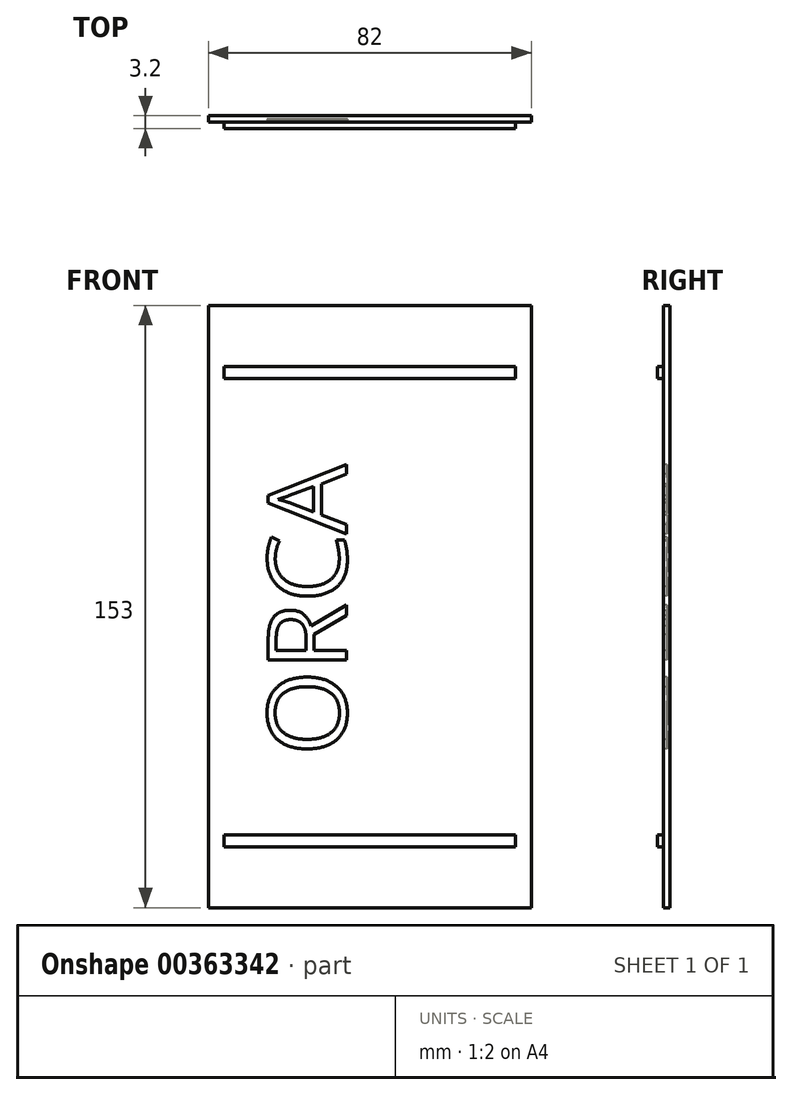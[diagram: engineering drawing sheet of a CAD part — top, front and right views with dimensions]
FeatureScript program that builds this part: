
annotation { "Feature Type Name" : "Feature", "Feature Type Description" : "" }
export const myFeature = defineFeature(function(context is Context, id is Id, definition is map)
    precondition{}
    {
        {
            var Q0;
            Q0=qCreatedBy(makeId("Front.planeOp"),FACE);
            var sketch = newSketch(context, id + "F0", { "sketchPlane" : qUnion([Q0])});
            skLineSegment(sketch, "E0", {"start": v(-82, 76.5) * mm, "end": v(0, 76.5) * mm});
            skLineSegment(sketch, "E1", {"start": v(0, 76.5) * mm, "end": v(0, -76.5) * mm});
            skLineSegment(sketch, "E2", {"start": v(0, -76.5) * mm, "end": v(-82, -76.5) * mm});
            skLineSegment(sketch, "E3", {"start": v(-82, -76.5) * mm, "end": v(-82, 76.5) * mm});
            skSolve(sketch);
        }
        {
            var Q0;
            Q0=qSketchRegion(id+"F0",true);
            extrude(context, id + "F1", {"entities" : qUnion([Q0]), "depth" : 1.6 * mm});
        }
        {
            var Q0;
            Q0=qCreatedBy(makeId("Front.planeOp"),FACE);
            cPlane(context, id + "F2", {"entities" : qUnion([Q0]), "cplaneType" : CPlaneType.OFFSET, "offset" : 1.6 * mm, "width" : 150 * mm, "height" : 150 * mm});
        }
        {
            var Q0;
            Q0=qCreatedBy(id+"F2.planeOp",FACE);
            var sketch = newSketch(context, id + "F3", { "sketchPlane" : qUnion([Q0])});
            skLineSegment(sketch, "E4", {"start": v(-4, 61) * mm, "end": v(-78, 61) * mm});
            skLineSegment(sketch, "E5", {"start": v(-4, 61) * mm, "end": v(-4, 58) * mm});
            skLineSegment(sketch, "E6", {"start": v(-4, 58) * mm, "end": v(-78, 58) * mm});
            skLineSegment(sketch, "E7", {"start": v(-78, 58) * mm, "end": v(-78, 61) * mm});
            skLineSegment(sketch, "E8.MirrorCS", {"start": v(-4, -58) * mm, "end": v(-78, -58) * mm});
            skLineSegment(sketch, "E9.MirrorCS", {"start": v(-4, -61) * mm, "end": v(-4, -58) * mm});
            skLineSegment(sketch, "E10.MirrorCS", {"start": v(-78, -58) * mm, "end": v(-78, -61) * mm});
            skLineSegment(sketch, "E11.MirrorCS", {"start": v(-4, -61) * mm, "end": v(-78, -61) * mm});
            skSolve(sketch);
        }
        {
            var Q0;
            Q0=qSketchRegion(id+"F3",true);
            extrude(context, id + "F4", {"entities" : qUnion([Q0]), "operationType" : NewBodyOperationType.ADD, "depth" : 1.6 * mm});
        }
        {
            var Q0;
            Q0=makeQuery(id+"F1.opExtrude","CAP_FACE",FACE,{"disambiguationData":[OSD([sQuery(id+"F0.wireOp",EDGE,"E0"),sQuery(id+"F0.wireOp",EDGE,"E1"),sQuery(id+"F0.wireOp",EDGE,"E2"),sQuery(id+"F0.wireOp",EDGE,"E3")])],"isStart":false});
            var sketch = newSketch(context, id + "F5", { "sketchPlane" : qUnion([Q0])});
            skText(sketch, "E12", { "text": "ORCA", "fontName": "OpenSans-Regular.ttf"});
            const initialGuessF5  = {"E12": [-0.047, -0.03785, 0, 1, 0.02]};
            skSetInitialGuess(sketch, initialGuessF5);
            skSolve(sketch);
        }
        {
            var Q0;
            Q0 = qSketchRegion(id + "F5", true);
            extrude(context, id + "F6", {"entities" : qUnion([Q0]), "operationType" : NewBodyOperationType.REMOVE, "oppositeDirection" : true, "depth" : .8 * mm});
        }
    });
